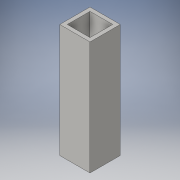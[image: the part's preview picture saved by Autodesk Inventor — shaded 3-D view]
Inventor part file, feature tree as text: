
AUTODESK INVENTOR PART (.ipt)
format: ipt  version: 2016 (Build 200138000, 138)  size: 94,208 bytes
history: native  units: in
note: dims shown in document units (in); Inventor stores cm internally (conversion verified against a paired STEP export)
features: extrude x1, sketch x1
ambient origin geometry x8: Origin, YZ Plane, XZ Plane, XY Plane, X Axis, Y Axis, Z Axis, Center Point
bodies: Solid1 (feature_tree)
feature tree (2):
  extrude  "Extrusion1"  Depth=1.0in
  sketch  "Sketch1"  dims[d0=1.0in d1=1.0in d2=0.125in d3=0.125in d4=0.125in d5=0.125in d6=3.75in d7=0.0in]
